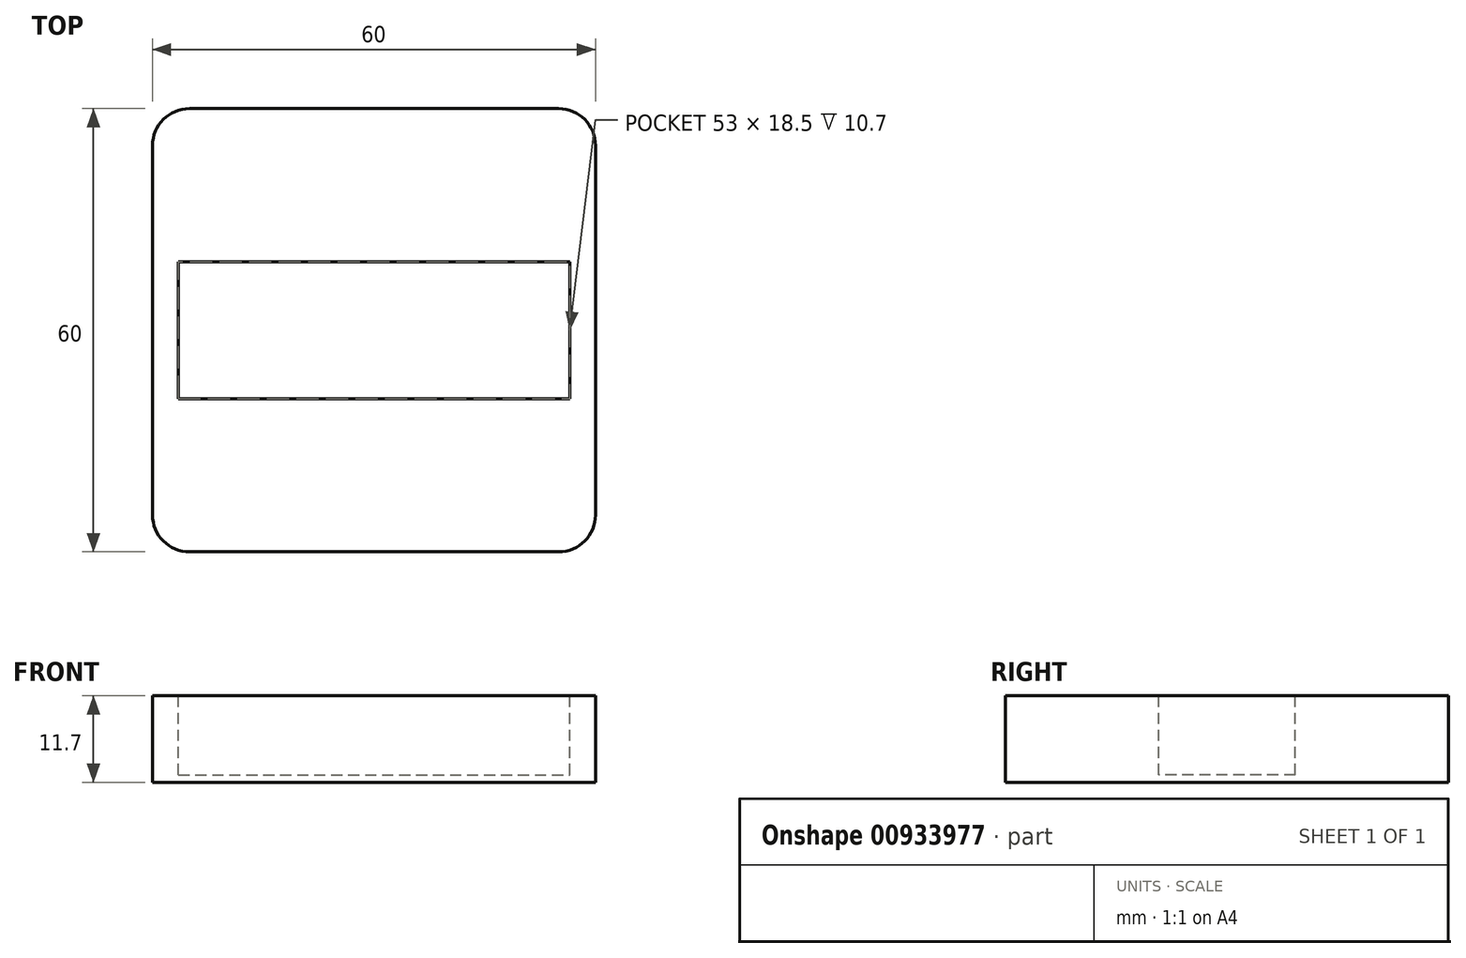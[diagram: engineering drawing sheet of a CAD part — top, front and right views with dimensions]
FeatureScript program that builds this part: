
annotation { "Feature Type Name" : "Feature", "Feature Type Description" : "" }
export const myFeature = defineFeature(function(context is Context, id is Id, definition is map)
    precondition{}
    {
        {
            var Q0;
            Q0=qCreatedBy(makeId("Top.planeOp"),FACE);
            var sketch = newSketch(context, id + "F0", { "sketchPlane" : qUnion([Q0])});
            skLineSegment(sketch, "E0.bottom", {"start": v(-30, 30) * mm, "end": v(30, 30) * mm});
            skLineSegment(sketch, "E0.top", {"start": v(-30, -30) * mm, "end": v(30, -30) * mm});
            skLineSegment(sketch, "E0.left", {"start": v(-30, 30) * mm, "end": v(-30, -30) * mm});
            skLineSegment(sketch, "E0.right", {"start": v(30, 30) * mm, "end": v(30, -30) * mm});
            skPoint(sketch, "E0.middle", {"position": v(0, 0) * mm});
            skSolve(sketch);
        }
        {
            var Q0;
            Q0=makeQuery(id+"F0.imprint","IMPRINT",FACE,{"disambiguationData":[TD([[makeQuery(id+"F0.imprint","IMPRINT",EDGE,{"derivedFrom":sQuery(id+"F0.wireOp",EDGE,"E0.bottom")}),-1.0]])]});
            extrude(context, id + "F1", {"entities" : qUnion([Q0]), "depth" : 11.7 * mm, "offsetDistance" : 25 * mm});
        }
        {
            var Q0;
            Q0=makeQuery(id+"F1.opExtrude","SWEPT_EDGE",EDGE,{"disambiguationData":[OSD([sQuery(id+"F0.wireOp",EDGE,"E0.bottom"),sQuery(id+"F0.wireOp",EDGE,"E0.left")])]});
            var Q1;
            Q1=makeQuery(id+"F1.opExtrude","SWEPT_EDGE",EDGE,{"disambiguationData":[OSD([sQuery(id+"F0.wireOp",EDGE,"E0.top"),sQuery(id+"F0.wireOp",EDGE,"E0.left")])]});
            var Q2;
            Q2=makeQuery(id+"F1.opExtrude","SWEPT_EDGE",EDGE,{"disambiguationData":[OSD([sQuery(id+"F0.wireOp",EDGE,"E0.bottom"),sQuery(id+"F0.wireOp",EDGE,"E0.right")])]});
            var Q3;
            Q3=makeQuery(id+"F1.opExtrude","SWEPT_EDGE",EDGE,{"disambiguationData":[OSD([sQuery(id+"F0.wireOp",EDGE,"E0.top"),sQuery(id+"F0.wireOp",EDGE,"E0.right")])]});
            fillet(context, id + "F2", {"entities" : qUnion([Q0, Q1, Q2, Q3]), "radius" : 5 * mm, "tangentPropagation" : true, "allowEdgeOverflow" : false});
        }
        {
            var Q0;
            Q0=makeQuery(id+"F1.opExtrude","CAP_FACE",FACE,{"disambiguationData":[OSD([sQuery(id+"F0.wireOp",EDGE,"E0.bottom"),sQuery(id+"F0.wireOp",EDGE,"E0.top"),sQuery(id+"F0.wireOp",EDGE,"E0.left"),sQuery(id+"F0.wireOp",EDGE,"E0.right")])],"isStart":false});
            var sketch = newSketch(context, id + "F3", { "sketchPlane" : qUnion([Q0])});
            skLineSegment(sketch, "E1.bottom", {"start": v(-26.5, 9.25) * mm, "end": v(26.5, 9.25) * mm});
            skLineSegment(sketch, "E1.top", {"start": v(-26.5, -9.25) * mm, "end": v(26.5, -9.25) * mm});
            skLineSegment(sketch, "E1.left", {"start": v(-26.5, 9.25) * mm, "end": v(-26.5, -9.25) * mm});
            skLineSegment(sketch, "E1.right", {"start": v(26.5, 9.25) * mm, "end": v(26.5, -9.25) * mm});
            skPoint(sketch, "E1.middle", {"position": v(0, 0) * mm});
            skSolve(sketch);
        }
        {
            var Q0;
            Q0=makeQuery(id+"F3.imprint","IMPRINT",FACE,{"disambiguationData":[TD([[makeQuery(id+"F3.imprint","IMPRINT",EDGE,{"derivedFrom":sQuery(id+"F3.wireOp",EDGE,"E1.bottom")}),-1.0]])]});
            extrude(context, id + "F4", {"entities" : qUnion([Q0]), "operationType" : NewBodyOperationType.REMOVE, "oppositeDirection" : true, "depth" : 10.7 * mm, "offsetDistance" : 25 * mm});
        }
    });
